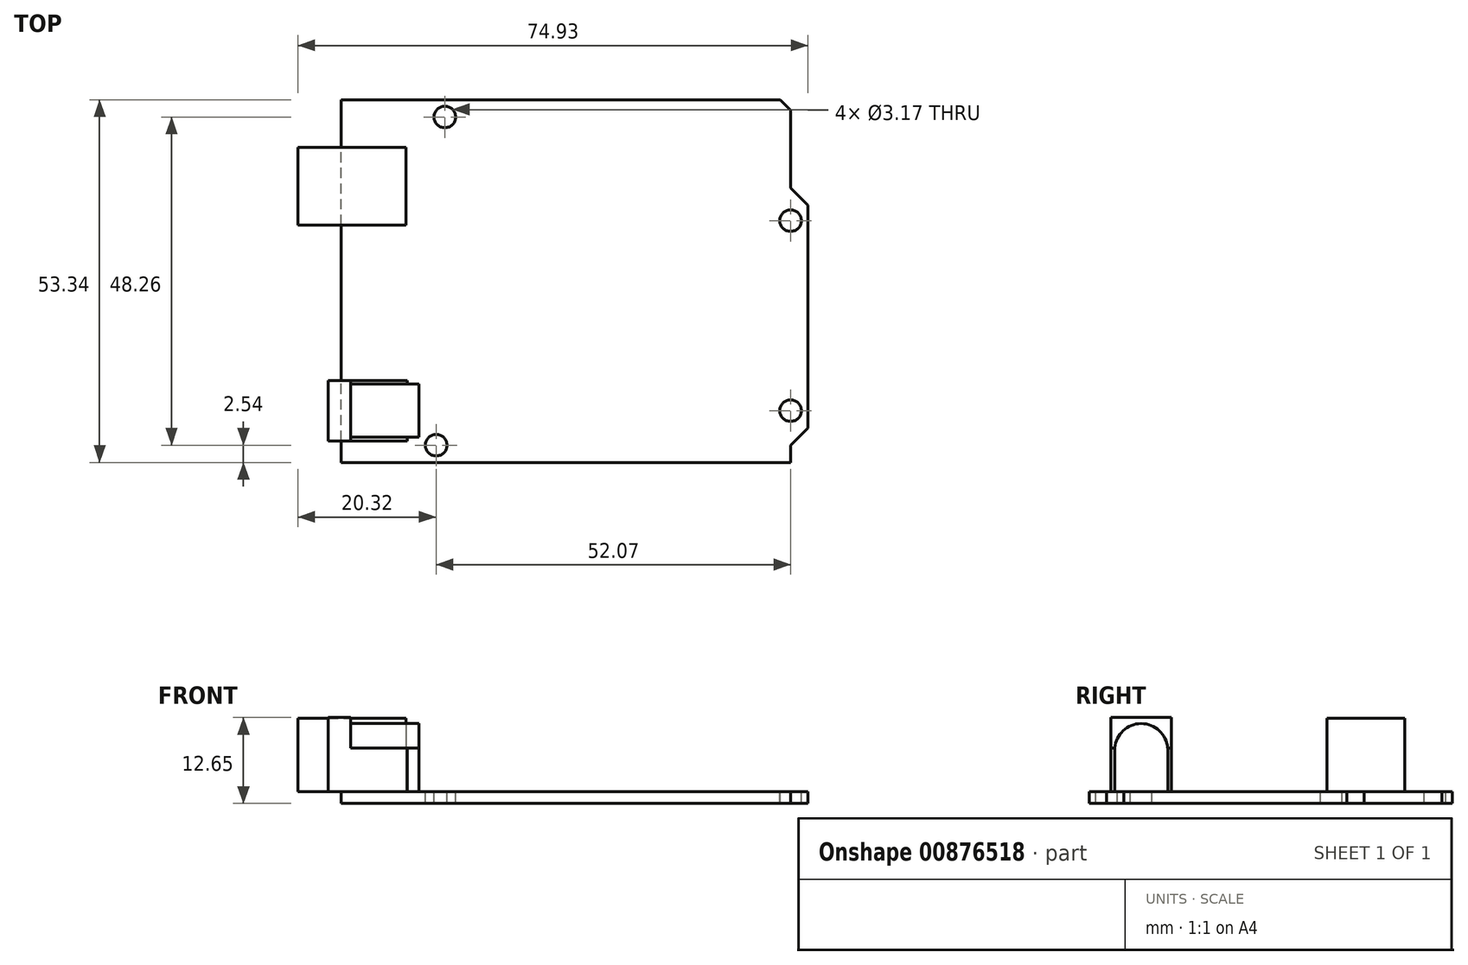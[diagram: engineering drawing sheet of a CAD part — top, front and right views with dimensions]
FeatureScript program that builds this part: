
annotation { "Feature Type Name" : "Feature", "Feature Type Description" : "" }
export const myFeature = defineFeature(function(context is Context, id is Id, definition is map)
    precondition{}
    {
        {
            var Q0;
            Q0=qCreatedBy(makeId("Top.planeOp"),FACE);
            var sketch = newSketch(context, id + "F0", { "sketchPlane" : qUnion([Q0])});
            skLineSegment(sketch, "E0", {"start": v(0, 0) * mm, "end": v(0, 53.34) * mm});
            skLineSegment(sketch, "E1", {"start": v(0, 53.34) * mm, "end": v(64.52, 53.34) * mm});
            skLineSegment(sketch, "E2", {"start": v(64.52, 53.34) * mm, "end": v(66.04, 51.82) * mm});
            skLineSegment(sketch, "E3", {"start": v(66.04, 51.82) * mm, "end": v(66.04, 40.39) * mm});
            skLineSegment(sketch, "E4", {"start": v(66.04, 40.39) * mm, "end": v(68.58, 37.85) * mm});
            skLineSegment(sketch, "E5", {"start": v(68.58, 37.85) * mm, "end": v(68.58, 5.08) * mm});
            skLineSegment(sketch, "E6", {"start": v(66.04, 0) * mm, "end": v(0, 0) * mm});
            skLineSegment(sketch, "E7", {"start": v(66.04, 0) * mm, "end": v(66.04, 2.54) * mm});
            skLineSegment(sketch, "E8", {"start": v(66.04, 2.54) * mm, "end": v(68.58, 5.08) * mm});
            skCircle(sketch, "E9", {"center": v(15.24, 50.8) * mm, "radius": 1.59 * mm});
            skCircle(sketch, "E10", {"center": v(13.97, 2.54) * mm, "radius": 1.59 * mm});
            skCircle(sketch, "E11", {"center": v(66.04, 7.62) * mm, "radius": 1.59 * mm});
            skCircle(sketch, "E12", {"center": v(66.04, 35.56) * mm, "radius": 1.59 * mm});
            skLineSegment(sketch, "E13.bottom", {"start": v(-1.9, 12.06) * mm, "end": v(11.43, 12.06) * mm});
            skLineSegment(sketch, "E13.top", {"start": v(-1.9, 3.17) * mm, "end": v(11.43, 3.17) * mm});
            skLineSegment(sketch, "E13.left", {"start": v(-1.9, 12.06) * mm, "end": v(-1.9, 3.17) * mm});
            skLineSegment(sketch, "E13.right", {"start": v(11.43, 12.06) * mm, "end": v(11.43, 3.17) * mm});
            skLineSegment(sketch, "E14.bottom", {"start": v(-6.35, 46.35) * mm, "end": v(9.53, 46.35) * mm});
            skLineSegment(sketch, "E14.top", {"start": v(-6.35, 34.92) * mm, "end": v(9.53, 34.92) * mm});
            skLineSegment(sketch, "E14.left", {"start": v(-6.35, 46.35) * mm, "end": v(-6.35, 34.92) * mm});
            skLineSegment(sketch, "E14.right", {"start": v(9.53, 46.35) * mm, "end": v(9.53, 34.92) * mm});
            skSolve(sketch);
        }
        {
            var Q0;
            {var subQ4=sQuery(id+"F0.wireOp",EDGE,"E1");Q0=makeQuery(id+"F0.imprint","IMPRINT",FACE,{"disambiguationData":[TD([[makeQuery(id+"F0.imprint","IMPRINT",EDGE,{"derivedFrom":subQ4}),-1.0]])]});}
            var Q1;
            {var subQ5=sQuery(id+"F0.wireOp",EDGE,"E13.right");Q1=makeQuery(id+"F0.imprint","IMPRINT",FACE,{"disambiguationData":[TD([[makeQuery(id+"F0.imprint","IMPRINT",EDGE,{"derivedFrom":subQ5}),-1.0]])]});}
            var Q2;
            {var subQ5=sQuery(id+"F0.wireOp",EDGE,"E14.right");Q2=makeQuery(id+"F0.imprint","IMPRINT",FACE,{"disambiguationData":[TD([[makeQuery(id+"F0.imprint","IMPRINT",EDGE,{"derivedFrom":subQ5}),-1.0]])]});}
            extrude(context, id + "F1", {"entities" : qUnion([Q0, Q1, Q2]), "oppositeDirection" : true, "depth" : 1.75 * mm, "offsetDistance" : 25 * mm});
        }
        {
            var Q0;
            {var subQ5=sQuery(id+"F0.wireOp",EDGE,"E14.left");Q0=makeQuery(id+"F0.imprint","IMPRINT",FACE,{"disambiguationData":[TD([[makeQuery(id+"F0.imprint","IMPRINT",EDGE,{"derivedFrom":subQ5}),1.0]])]});}
            var Q1;
            {var subQ5=sQuery(id+"F0.wireOp",EDGE,"E14.right");Q1=makeQuery(id+"F0.imprint","IMPRINT",FACE,{"disambiguationData":[TD([[makeQuery(id+"F0.imprint","IMPRINT",EDGE,{"derivedFrom":subQ5}),-1.0]])]});}
            extrude(context, id + "F2", {"entities" : qUnion([Q0, Q1]), "operationType" : NewBodyOperationType.ADD, "depth" : 10.8 * mm, "offsetDistance" : 25 * mm});
        }
        {
            var Q0;
            {var subQ5=sQuery(id+"F0.wireOp",EDGE,"E13.right");Q0=makeQuery(id+"F0.imprint","IMPRINT",FACE,{"disambiguationData":[TD([[makeQuery(id+"F0.imprint","IMPRINT",EDGE,{"derivedFrom":subQ5}),-1.0]])]});}
            var Q1;
            {var subQ5=sQuery(id+"F0.wireOp",EDGE,"E13.left");Q1=makeQuery(id+"F0.imprint","IMPRINT",FACE,{"disambiguationData":[TD([[makeQuery(id+"F0.imprint","IMPRINT",EDGE,{"derivedFrom":subQ5}),1.0]])]});}
            extrude(context, id + "F3", {"entities" : qUnion([Q0, Q1]), "operationType" : NewBodyOperationType.ADD, "depth" : 10.9 * mm, "offsetDistance" : 25 * mm});
        }
        {
            var Q0;
            Q0=makeQuery(id+"F3.opExtrude","SWEPT_FACE",FACE,{"disambiguationData":[OSD([sQuery(id+"F0.wireOp",EDGE,"E13.right")])]});
            var sketch = newSketch(context, id + "F4", { "sketchPlane" : qUnion([Q0])});
            skLineSegment(sketch, "E15.bottom", {"start": v(3.17, 0) * mm, "end": v(12.06, 0) * mm});
            skLineSegment(sketch, "E15.top", {"start": v(3.17, 10.9) * mm, "end": v(12.06, 10.9) * mm});
            skLineSegment(sketch, "E15.left", {"start": v(3.17, 0) * mm, "end": v(3.17, 10.9) * mm});
            skLineSegment(sketch, "E15.right", {"start": v(12.06, 0) * mm, "end": v(12.06, 10.9) * mm});
            skLineSegment(sketch, "E16.bottom", {"start": v(11.52, 0) * mm, "end": v(3.72, 0) * mm});
            skLineSegment(sketch, "E16.top", {"start": v(11.52, 10) * mm, "end": v(3.72, 10) * mm});
            skLineSegment(sketch, "E16.left", {"start": v(11.52, 0) * mm, "end": v(11.52, 10) * mm});
            skLineSegment(sketch, "E16.right", {"start": v(3.72, 0) * mm, "end": v(3.72, 10) * mm});
            skPoint(sketch, "E16.middle", {"position": v(7.62, 5) * mm});
            skPoint(sketch, "E16.middle.positionSnap0", {"position": v(7.62, 0) * mm});
            skPoint(sketch, "E16.centerSnap0", {"position": v(7.62, 0) * mm});
            skLineSegment(sketch, "E17", {"start": v(3.72, 6.4) * mm, "end": v(11.52, 6.4) * mm, "construction": true});
            skCircle(sketch, "E18", {"center": v(7.62, 6.1) * mm, "radius": 3.9 * mm});
            skLineSegment(sketch, "E19", {"start": v(7.62, 6.1) * mm, "end": v(7.62, 10) * mm, "construction": true});
            skLineSegment(sketch, "E20", {"start": v(3.73, 6.4) * mm, "end": v(3.17, 6.4) * mm});
            skLineSegment(sketch, "E21", {"start": v(11.5, 6.4) * mm, "end": v(12.06, 6.4) * mm});
            skSolve(sketch);
        }
        {
            var Q0;
            {var subQ4=sQuery(id+"F4.wireOp",EDGE,"E15.right");var subQ5=sQuery(id+"F4.wireOp",EDGE,"E15.bottom");var subQ6=makeQuery(id+"F4.imprint","INTERSECT",VERTEX,{"derivedFrom":[subQ5,subQ4]});Q0=makeQuery(id+"F4.imprint","IMPRINT",FACE,{"disambiguationData":[TD([[makeQuery(id+"F4.imprint","IMPRINT",EDGE,{"disambiguationData":[TD([[subQ6,1.0]])],"derivedFrom":subQ4}),-1.0]])]});}
            var Q1;
            {var subQ1=sQuery(id+"F4.wireOp",EDGE,"E15.top");Q1=makeQuery(id+"F4.imprint","IMPRINT",FACE,{"disambiguationData":[TD([[makeQuery(id+"F4.imprint","IMPRINT",EDGE,{"derivedFrom":subQ1}),1.0]])]});}
            var Q2;
            {var subQ0=sQuery(id+"F4.wireOp",EDGE,"E16.left");var subQ1=sQuery(id+"F4.wireOp",EDGE,"E16.top");var subQ2=makeQuery(id+"F4.imprint","INTERSECT",VERTEX,{"derivedFrom":[subQ1,subQ0]});Q2=makeQuery(id+"F4.imprint","IMPRINT",FACE,{"disambiguationData":[TD([[makeQuery(id+"F4.imprint","IMPRINT",EDGE,{"disambiguationData":[TD([[subQ2,-1.0]])],"derivedFrom":subQ1}),1.0]])]});}
            var Q3;
            {var subQ0=sQuery(id+"F4.wireOp",EDGE,"E16.right");var subQ1=sQuery(id+"F4.wireOp",EDGE,"E16.top");var subQ2=makeQuery(id+"F4.imprint","INTERSECT",VERTEX,{"derivedFrom":[subQ1,subQ0]});Q3=makeQuery(id+"F4.imprint","IMPRINT",FACE,{"disambiguationData":[TD([[makeQuery(id+"F4.imprint","IMPRINT",EDGE,{"disambiguationData":[TD([[subQ2,1.0]])],"derivedFrom":subQ1}),1.0]])]});}
            var Q4;
            {var subQ1=sQuery(id+"F4.wireOp",EDGE,"E15.bottom");var subQ6=sQuery(id+"F4.wireOp",EDGE,"E15.left");var subQ7=makeQuery(id+"F4.imprint","INTERSECT",VERTEX,{"derivedFrom":[subQ1,subQ6]});Q4=makeQuery(id+"F4.imprint","IMPRINT",FACE,{"disambiguationData":[TD([[makeQuery(id+"F4.imprint","IMPRINT",EDGE,{"disambiguationData":[TD([[subQ7,1.0]])],"derivedFrom":subQ6}),1.0]])]});}
            extrude(context, id + "F5", {"entities" : qUnion([Q0, Q1, Q2, Q3, Q4]), "operationType" : NewBodyOperationType.REMOVE, "oppositeDirection" : true, "depth" : 1.7 * mm, "offsetDistance" : 25 * mm});
        }
        {
            var Q0;
            {var subQ0=sQuery(id+"F4.wireOp",EDGE,"E16.right");var subQ1=sQuery(id+"F4.wireOp",EDGE,"E16.top");var subQ2=makeQuery(id+"F4.imprint","INTERSECT",VERTEX,{"derivedFrom":[subQ1,subQ0]});Q0=makeQuery(id+"F4.imprint","IMPRINT",FACE,{"disambiguationData":[TD([[makeQuery(id+"F4.imprint","IMPRINT",EDGE,{"disambiguationData":[TD([[subQ2,1.0]])],"derivedFrom":subQ1}),1.0]])]});}
            var Q1;
            {var subQ0=sQuery(id+"F4.wireOp",EDGE,"E16.left");var subQ1=sQuery(id+"F4.wireOp",EDGE,"E16.top");var subQ2=makeQuery(id+"F4.imprint","INTERSECT",VERTEX,{"derivedFrom":[subQ1,subQ0]});Q1=makeQuery(id+"F4.imprint","IMPRINT",FACE,{"disambiguationData":[TD([[makeQuery(id+"F4.imprint","IMPRINT",EDGE,{"disambiguationData":[TD([[subQ2,-1.0]])],"derivedFrom":subQ1}),1.0]])]});}
            var Q2;
            {var subQ1=sQuery(id+"F4.wireOp",EDGE,"E15.top");Q2=makeQuery(id+"F4.imprint","IMPRINT",FACE,{"disambiguationData":[TD([[makeQuery(id+"F4.imprint","IMPRINT",EDGE,{"derivedFrom":subQ1}),1.0]])]});}
            extrude(context, id + "F6", {"entities" : qUnion([Q0, Q1, Q2]), "operationType" : NewBodyOperationType.REMOVE, "oppositeDirection" : true, "depth" : 10 * mm, "offsetDistance" : 25 * mm});
        }
    });
